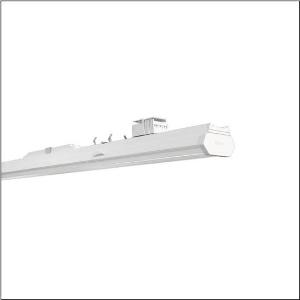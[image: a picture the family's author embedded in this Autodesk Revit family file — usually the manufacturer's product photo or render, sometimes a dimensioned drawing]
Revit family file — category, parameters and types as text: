
# Revit family: licross_21_protected_mo_52td12mn4a5g
name_source: partatom
category: Lighting Fixtures
units: mm (PartAtom-declared; Revit-internal decimal feet)

## family parameters
Cut with Voids When Loaded = No
Host = Face
Light Source = No
Part Type = Normal
Room Calculation Point = No
Round Connector Dimension = Use Diameter
Shared = No

## types (1)
- --- (1 x LED, 10750 lm, 60.5 W, 4000K)
    Apparent Load = 61 VA
    CIE Flux Codes = 73 92 98 99 100
    Color Rendering = 80
    Color Temperature = 4000K
    Default Elevation = 1800 mm
    Description = Licross 21 Protected MO, luminaire insert, of sheet steel, galvanised, coil coated, white, length: 1.500mm, width: 90mm, height: 101mm, LED rated luminous flux: 10.750lm, light colour: 840, SDCM (Standard Deviation of Colour Matching)MacAdam ≤ 3 SDCM (initial), control gear: ON/OFF Multilumen, with plug, 3-pole, with phase selection, mains connection: 220..240V, AC, 50/60Hz, rated input power: 61W, internal wiring halogen-free, primary light control with lens, of plastic, primary optical cover: cover, of PMMA, light emission: direct distribution, primary light characteristic: symmetric, protection rating (complete): IP54, insulation class (complete): insulation class I (protective earthing), certification: CE, ENEC, VDE, UKCA, protection symbol: D if used in an environment with non-conductive dust loads with corresponding accessories, impact resistance: IK06, permissible ambient temperature for indoor applications: -35..+45°C, corresponds to IFS (International Featured Standards) requirements for safety and quality in the food industry, reducing of maximum allowable ambient temperature of 5°C with ceiling mounting, LABS conformity tested according to VDMA 24364:2018-05, The light source and the operating device comply with the requirements of the Ecodesign Regulation (EU) 2019/2020 and are replaceable in accordance with this regulation, packaging unit: 1 piece
    Height = 92 mm
    Lamp = 1 x LED
    Lamp Light Flux = 10750 lm
    Lamp Power = 60.5 W
    Lamp count = 1
    Length = 1500 mm
    Luminous efficacy = 178 lm/W
    Manufacturer = Siteco
    ModVariant = No
    Model = 52TD12MN4A5G
    Mounting Place = Ceiling
    Mounting Type = Pendant
    Number of Poles = 1
    OnlyDefault = Yes
    Power Factor = 1
    Product Name = Licross 21 Protected MO
    Product group = luminaire insert | ceiling pendant
    ProductGroupID = 901
    Protection Class = Protection class I
    Protection Degree = IP 54
    RLX_Detail_Level = 1
    RLX_Emergency_Light_Flux = 0 lm
    RLX_Emergency_Type = 0
    RLX_Emergency_Type_DB = No
    RlxData = <blob elided: 22325 chars, md5=29bd4e0f>
    Socket = socket
    Standby Power = 0 W
    System Light Flux = 10750 lm
    System Power = 61 W
    Type Comments = factory setting: luminous flux: 100 % | (A | C | E) | 140 mA
    Type Image = l_1256148.jpg
    URL = http://relux.com
    VarID = @adj_110643
    Voltage = 0 V
    Weight = 0.00 kg
    Width = 88 mm

## geometry (parser evidence)
native form markers: Blend x4, Sweep x9
no freeform markers — native parametric forms only
